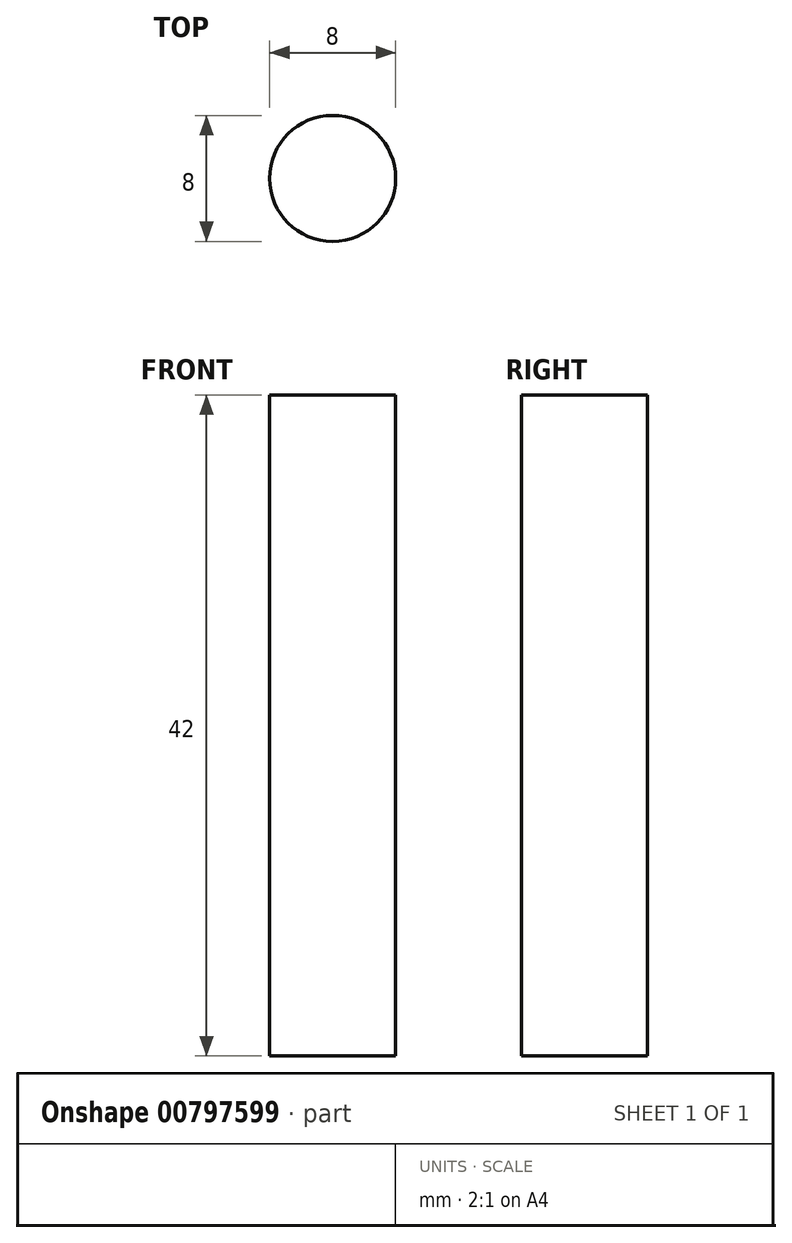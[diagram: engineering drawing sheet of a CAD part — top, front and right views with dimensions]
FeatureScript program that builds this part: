
annotation { "Feature Type Name" : "Feature", "Feature Type Description" : "" }
export const myFeature = defineFeature(function(context is Context, id is Id, definition is map)
    precondition{}
    {
        {
            var Q0;
            Q0=qCreatedBy(makeId("Top.planeOp"),FACE);
            var sketch = newSketch(context, id + "F0", { "sketchPlane" : qUnion([Q0])});
            skCircle(sketch, "E0", {"center": v(0, 0) * mm, "radius": 4 * mm});
            skSolve(sketch);
        }
        {
            var Q0;
            Q0=makeQuery(id+"F0.imprint","IMPRINT",FACE,{"disambiguationData":[TD([[makeQuery(id+"F0.imprint","IMPRINT",EDGE,{"derivedFrom":sQuery(id+"F0.wireOp",EDGE,"E0")}),1.0]])]});
            extrude(context, id + "F1", {"entities" : qUnion([Q0]), "depth" : 42 * mm, "offsetDistance" : 25 * mm});
        }
        {
            var Q0;
            Q0=makeQuery(id+"F1.opExtrude","SWEPT_BODY",BODY,{"disambiguationData":[OSD([sQuery(id+"F0.wireOp",EDGE,"E0")])]});
            var Q1;
            Q1=makeQuery(id+"F1.opExtrude","SWEPT_FACE",FACE,{"disambiguationData":[OSD([sQuery(id+"F0.wireOp",EDGE,"E0")])]});
            transform(context, id + "F2", {"entities" : qUnion([Q0]), "transformType" : TransformType.TRANSLATION_DISTANCE, "transformDirection" : qUnion([Q1]), "distance" : 12 * mm, "makeCopy" : false});
        }
    });
